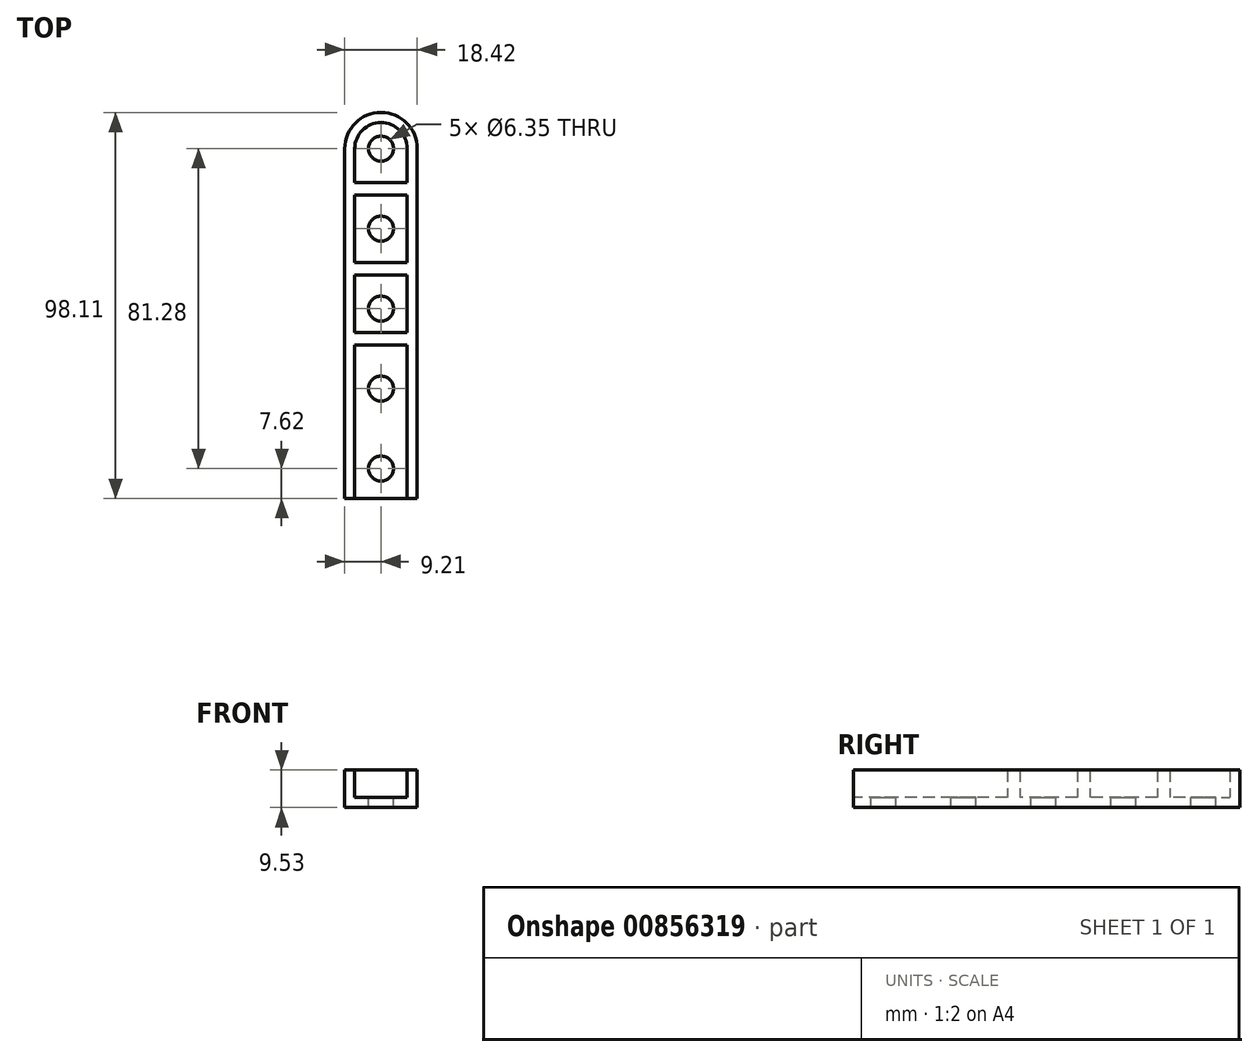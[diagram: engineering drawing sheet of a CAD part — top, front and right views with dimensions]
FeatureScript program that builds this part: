
annotation { "Feature Type Name" : "Feature", "Feature Type Description" : "" }
export const myFeature = defineFeature(function(context is Context, id is Id, definition is map)
    precondition{}
    {
        {
            var Q0;
            Q0=qCreatedBy(makeId("Top.planeOp"),FACE);
            var sketch = newSketch(context, id + "F0", { "sketchPlane" : qUnion([Q0])});
            skLineSegment(sketch, "E0.top", {"start": v(-9.2, 0) * mm, "end": v(9.2, 0) * mm});
            skLineSegment(sketch, "E0.left", {"start": v(-9.2, 88.9) * mm, "end": v(-9.2, 0) * mm});
            skLineSegment(sketch, "E0.right", {"start": v(9.2, 88.9) * mm, "end": v(9.2, 0) * mm});
            skArc(sketch, "E1", {"start": v(9.2, 88.9) * mm, "mid": v(0, 98.1) * mm, "end": v(-9.2, 88.9) * mm});
            skSolve(sketch);
        }
        {
            var Q0;
            Q0=makeQuery(id+"F0.imprint","IMPRINT",FACE,{"disambiguationData":[TD([[makeQuery(id+"F0.imprint","IMPRINT",EDGE,{"derivedFrom":sQuery(id+"F0.wireOp",EDGE,"E0.top")}),1.0]])]});
            extrude(context, id + "F1", {"entities" : qUnion([Q0]), "depth" : 9.52 * mm, "offsetDistance" : 25.4 * mm});
        }
        {
            var Q0;
            Q0=makeQuery(id+"F1.opExtrude","CAP_FACE",FACE,{"disambiguationData":[OSD([sQuery(id+"F0.wireOp",EDGE,"E0.top"),sQuery(id+"F0.wireOp",EDGE,"E0.left"),sQuery(id+"F0.wireOp",EDGE,"E0.right"),sQuery(id+"F0.wireOp",EDGE,"E1")])],"isStart":false});
            shell(context, id + "F2", {"entities" : qUnion([Q0]), "thickness" : 2.54 * mm});
        }
        {
            var Q0;
            Q0=makeQuery(id+"F1.opExtrude","CAP_FACE",FACE,{"disambiguationData":[OSD([sQuery(id+"F0.wireOp",EDGE,"E0.top"),sQuery(id+"F0.wireOp",EDGE,"E0.left"),sQuery(id+"F0.wireOp",EDGE,"E0.right"),sQuery(id+"F0.wireOp",EDGE,"E1")])],"isStart":false});
            var sketch = newSketch(context, id + "F3", { "sketchPlane" : qUnion([Q0])});
            skLineSegment(sketch, "E2.bottom", {"start": v(-6.67, 2.54) * mm, "end": v(6.67, 2.54) * mm});
            skLineSegment(sketch, "E2.top", {"start": v(-6.67, 0) * mm, "end": v(6.67, 0) * mm});
            skLineSegment(sketch, "E2.left", {"start": v(-6.67, 2.54) * mm, "end": v(-6.67, 0) * mm});
            skLineSegment(sketch, "E2.right", {"start": v(6.67, 2.54) * mm, "end": v(6.67, 0) * mm});
            skSolve(sketch);
        }
        {
            var Q0;
            Q0=makeQuery(id+"F3.imprint","IMPRINT",FACE,{"disambiguationData":[TD([[makeQuery(id+"F3.imprint","IMPRINT",EDGE,{"derivedFrom":sQuery(id+"F3.wireOp",EDGE,"E2.bottom")}),-1.0]])]});
            var Q1;
            Q1=makeQuery(id+"F2.opShell","OFFSET_FACE",FACE,{"disambiguationData":[OSD([sQuery(id+"F0.wireOp",EDGE,"E0.top"),sQuery(id+"F0.wireOp",EDGE,"E0.left"),sQuery(id+"F0.wireOp",EDGE,"E0.right"),sQuery(id+"F0.wireOp",EDGE,"E1")])]});
            extrude(context, id + "F4", {"entities" : qUnion([Q0]), "operationType" : NewBodyOperationType.REMOVE, "endBound" : BoundingType.UP_TO_SURFACE, "oppositeDirection" : true, "depth" : 25.4 * mm, "endBoundEntityFace" : qUnion([Q1]), "offsetDistance" : 25.4 * mm});
        }
        {
            var Q0;
            {var subQ0=sQuery(id+"F0.wireOp",EDGE,"E1");var subQ1=sQuery(id+"F0.wireOp",EDGE,"E0.right");var subQ2=sQuery(id+"F0.wireOp",EDGE,"E0.left");var subQ3=sQuery(id+"F0.wireOp",EDGE,"E0.top");Q0=makeQuery(id+"F4.boolean.opBoolean","MERGE",FACE,{"derivedFrom":[makeQuery(id+"F2.opShell","OFFSET_FACE",FACE,{"disambiguationData":[OSD([subQ3,subQ2,subQ1,subQ0])]}),makeQuery(id+"F4.opExtrude","CAP_FACE",FACE,{"disambiguationData":[OSD([subQ3,subQ2,subQ1,subQ0])],"isStart":false})]});}
            var sketch = newSketch(context, id + "F5", { "sketchPlane" : qUnion([Q0])});
            skCircle(sketch, "E3", {"center": v(0, 27.94) * mm, "radius": 3.18 * mm});
            skCircle(sketch, "E4", {"center": v(0, 48.26) * mm, "radius": 3.18 * mm});
            skCircle(sketch, "E5", {"center": v(0, 68.58) * mm, "radius": 3.18 * mm});
            skCircle(sketch, "E6", {"center": v(0, 88.9) * mm, "radius": 3.18 * mm});
            skCircle(sketch, "E7", {"center": v(0, 7.62) * mm, "radius": 3.18 * mm});
            skSolve(sketch);
        }
        {
            var Q0;
            Q0=makeQuery(id+"F5.imprint","IMPRINT",FACE,{"disambiguationData":[TD([[makeQuery(id+"F5.imprint","IMPRINT",EDGE,{"derivedFrom":sQuery(id+"F5.wireOp",EDGE,"E6")}),1.0]])]});
            var Q1;
            Q1=makeQuery(id+"F5.imprint","IMPRINT",FACE,{"disambiguationData":[TD([[makeQuery(id+"F5.imprint","IMPRINT",EDGE,{"derivedFrom":sQuery(id+"F5.wireOp",EDGE,"E5")}),1.0]])]});
            var Q2;
            Q2=makeQuery(id+"F5.imprint","IMPRINT",FACE,{"disambiguationData":[TD([[makeQuery(id+"F5.imprint","IMPRINT",EDGE,{"derivedFrom":sQuery(id+"F5.wireOp",EDGE,"E4")}),1.0]])]});
            var Q3;
            Q3=makeQuery(id+"F5.imprint","IMPRINT",FACE,{"disambiguationData":[TD([[makeQuery(id+"F5.imprint","IMPRINT",EDGE,{"derivedFrom":sQuery(id+"F5.wireOp",EDGE,"E3")}),1.0]])]});
            var Q4;
            Q4=makeQuery(id+"F5.imprint","IMPRINT",FACE,{"disambiguationData":[TD([[makeQuery(id+"F5.imprint","IMPRINT",EDGE,{"derivedFrom":sQuery(id+"F5.wireOp",EDGE,"E7")}),1.0]])]});
            extrude(context, id + "F6", {"entities" : qUnion([Q0, Q1, Q2, Q3, Q4]), "operationType" : NewBodyOperationType.REMOVE, "endBound" : BoundingType.THROUGH_ALL, "oppositeDirection" : true, "depth" : 25.4 * mm, "offsetDistance" : 25.4 * mm});
        }
        {
            var Q0;
            {var subQ0=sQuery(id+"F0.wireOp",EDGE,"E1");var subQ1=sQuery(id+"F0.wireOp",EDGE,"E0.right");var subQ2=sQuery(id+"F0.wireOp",EDGE,"E0.left");var subQ3=sQuery(id+"F0.wireOp",EDGE,"E0.top");Q0=makeQuery(id+"F4.boolean.opBoolean","MERGE",FACE,{"derivedFrom":[makeQuery(id+"F2.opShell","OFFSET_FACE",FACE,{"disambiguationData":[OSD([subQ3,subQ2,subQ1,subQ0])]}),makeQuery(id+"F4.opExtrude","CAP_FACE",FACE,{"disambiguationData":[OSD([subQ3,subQ2,subQ1,subQ0])],"isStart":false})]});}
            var sketch = newSketch(context, id + "F7", { "sketchPlane" : qUnion([Q0])});
            skLineSegment(sketch, "E8.bottom", {"start": v(-6.67, 80.33) * mm, "end": v(6.67, 80.33) * mm});
            skLineSegment(sketch, "E8.top", {"start": v(-6.67, 77.15) * mm, "end": v(6.67, 77.15) * mm});
            skLineSegment(sketch, "E8.left", {"start": v(-6.67, 80.33) * mm, "end": v(-6.67, 77.15) * mm});
            skLineSegment(sketch, "E8.right", {"start": v(6.67, 80.33) * mm, "end": v(6.67, 77.15) * mm});
            skLineSegment(sketch, "E9.bottom", {"start": v(-6.67, 60) * mm, "end": v(6.67, 60) * mm});
            skLineSegment(sketch, "E9.top", {"start": v(-6.67, 56.83) * mm, "end": v(6.67, 56.83) * mm});
            skLineSegment(sketch, "E9.left", {"start": v(-6.67, 60) * mm, "end": v(-6.67, 56.83) * mm});
            skLineSegment(sketch, "E9.right", {"start": v(6.67, 60) * mm, "end": v(6.67, 56.83) * mm});
            skLineSegment(sketch, "E10.bottom", {"start": v(-6.67, 42.23) * mm, "end": v(6.67, 42.23) * mm});
            skLineSegment(sketch, "E10.top", {"start": v(-6.67, 39.05) * mm, "end": v(6.67, 39.05) * mm});
            skLineSegment(sketch, "E10.left", {"start": v(-6.67, 42.23) * mm, "end": v(-6.67, 39.05) * mm});
            skLineSegment(sketch, "E10.right", {"start": v(6.67, 42.23) * mm, "end": v(6.67, 39.05) * mm});
            skSolve(sketch);
        }
        {
            var Q0;
            Q0=makeQuery(id+"F7.imprint","IMPRINT",FACE,{"disambiguationData":[TD([[makeQuery(id+"F7.imprint","IMPRINT",EDGE,{"derivedFrom":sQuery(id+"F7.wireOp",EDGE,"E8.bottom")}),-1.0]])]});
            var Q1;
            Q1=makeQuery(id+"F7.imprint","IMPRINT",FACE,{"disambiguationData":[TD([[makeQuery(id+"F7.imprint","IMPRINT",EDGE,{"derivedFrom":sQuery(id+"F7.wireOp",EDGE,"E9.bottom")}),-1.0]])]});
            var Q2;
            Q2=makeQuery(id+"F7.imprint","IMPRINT",FACE,{"disambiguationData":[TD([[makeQuery(id+"F7.imprint","IMPRINT",EDGE,{"derivedFrom":sQuery(id+"F7.wireOp",EDGE,"E10.bottom")}),-1.0]])]});
            var Q3;
            Q3=makeQuery(id+"F1.opExtrude","CAP_FACE",FACE,{"disambiguationData":[OSD([sQuery(id+"F0.wireOp",EDGE,"E0.top"),sQuery(id+"F0.wireOp",EDGE,"E0.left"),sQuery(id+"F0.wireOp",EDGE,"E0.right"),sQuery(id+"F0.wireOp",EDGE,"E1")])],"isStart":false});
            extrude(context, id + "F8", {"entities" : qUnion([Q0, Q1, Q2]), "operationType" : NewBodyOperationType.ADD, "endBound" : BoundingType.UP_TO_SURFACE, "depth" : 25.4 * mm, "endBoundEntityFace" : qUnion([Q3]), "offsetDistance" : 25.4 * mm});
        }
    });
